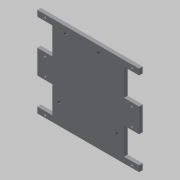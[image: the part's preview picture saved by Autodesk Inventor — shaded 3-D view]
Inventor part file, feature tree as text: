
AUTODESK INVENTOR PART (.ipt)
format: ipt  version: 2014 SP2 (Build 180246200, 246)  size: 141,312 bytes
history: native  units: mm
features: other x6, sketch x2, extrude x1, hole x1
ambient origin geometry x8: Origin, YZ Plane, XZ Plane, XY Plane, X Axis, Y Axis, Z Axis, Center Point
bodies: Solid1 (feature_tree)
feature tree (10):
  other  "Blocks"
  extrude  "Extrusion1"  Depth=22.53mm
  hole  "Hole1"  [1 undecoded]
  sketch  "Sketch1"  dims[d0=32.36mm d2=2.178mm d3=2.096mm d4=22.53mm d5=2.096mm d6=2.178mm]
  other  "Servo Hole"
  sketch  "Sketch2"  dims[d8=85.196mm d9=75.0mm d10=3.0mm d11=0.0mm d12=60.0mm d18=3.0mm d19=2.54mm d20=13.97mm d21=53.34mm d22=68.58mm d23=3.0mm d24=7.62mm d25=2.54mm d28=3.0mm d29=2.54mm d30=15.24mm d31=3.0mm d32=27.94mm d33=2.459mm d34=6.0mm d35=4.0mm d36=2.0mm d37=90.0deg d38=8.0mm d39=20.594885mm]
  other  "Servo Hole:1"
  other  "Servo Hole:2"
  other  "Servo Hole:3"
  other  "Servo Hole:4"
note: 1 required parameter value undecoded (feature->parameter linkage not recoverable at this tier; creation-order binding heuristic only, values carry confidence <= 0.55)
